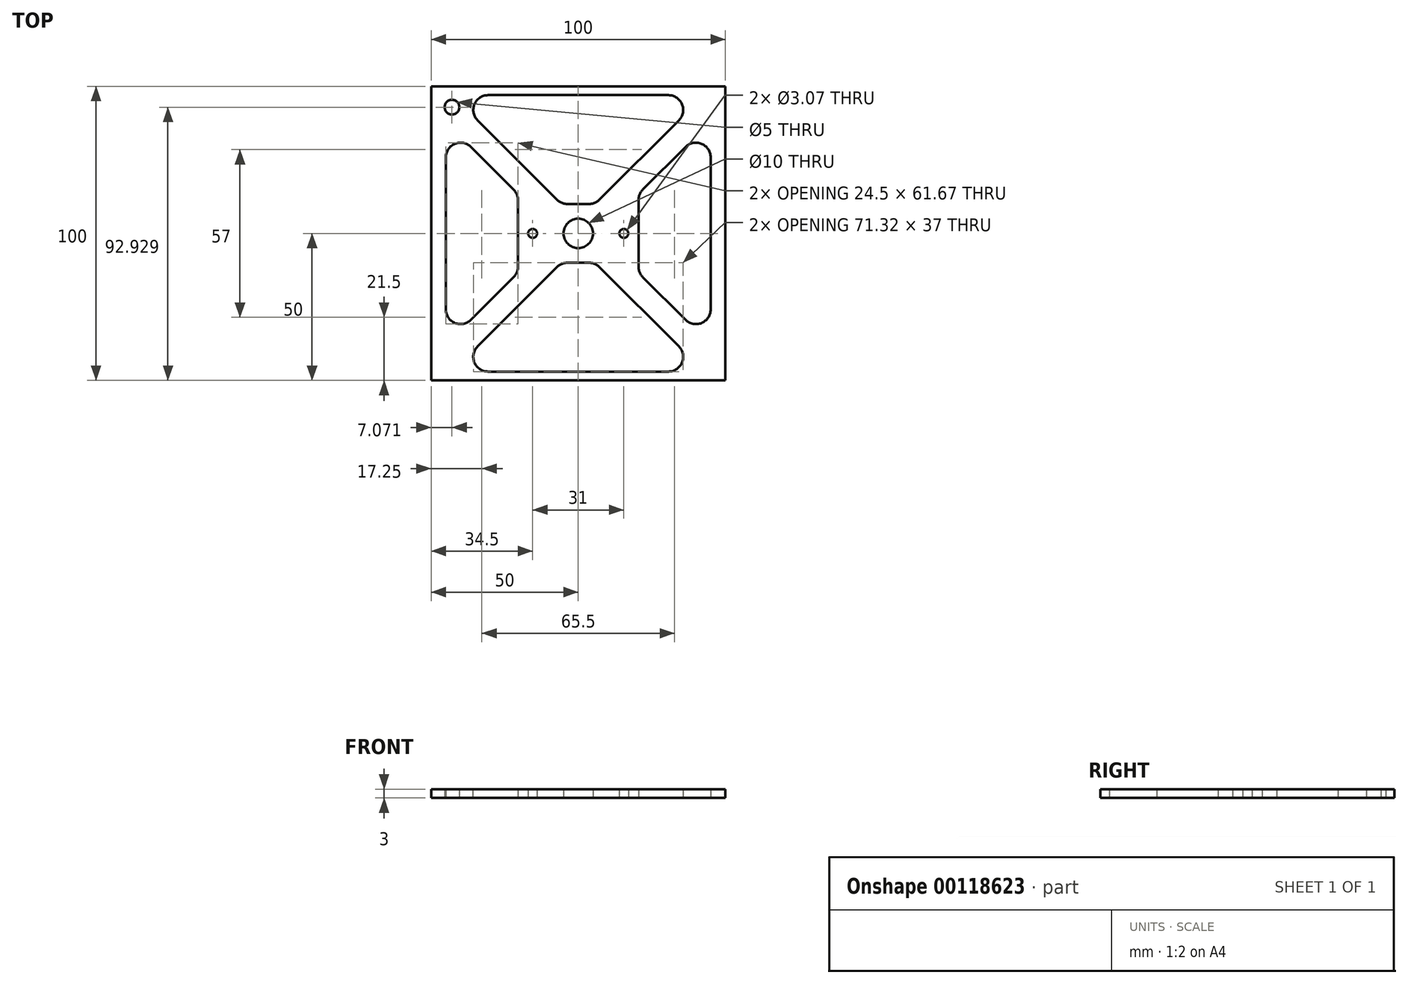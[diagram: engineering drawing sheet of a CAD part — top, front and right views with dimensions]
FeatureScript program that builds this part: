
annotation { "Feature Type Name" : "Feature", "Feature Type Description" : "" }
export const myFeature = defineFeature(function(context is Context, id is Id, definition is map)
    precondition{}
    {
        {
            var Q0;
            Q0=qCreatedBy(makeId("Top.planeOp"),FACE);
            var sketch = newSketch(context, id + "F0", { "sketchPlane" : qUnion([Q0])});
            skLineSegment(sketch, "E0.bottom", {"start": v(50, -50) * mm, "end": v(-50, -50) * mm});
            skLineSegment(sketch, "E0.top", {"start": v(50, 50) * mm, "end": v(-50, 50) * mm});
            skLineSegment(sketch, "E0.left", {"start": v(50, -50) * mm, "end": v(50, 50) * mm});
            skLineSegment(sketch, "E0.right", {"start": v(-50, -50) * mm, "end": v(-50, 50) * mm});
            skPoint(sketch, "E0.middle", {"position": v(0, 0) * mm});
            skCircle(sketch, "E1", {"center": v(0, 0) * mm, "radius": 5 * mm});
            skLineSegment(sketch, "E2", {"start": v(0, 0) * mm, "end": v(15.5, 0) * mm, "construction": true});
            skLineSegment(sketch, "E3", {"start": v(0, 0) * mm, "end": v(-15.5, 0) * mm, "construction": true});
            skCircle(sketch, "E4", {"center": v(-15.5, 0) * mm, "radius": 1.53 * mm});
            skCircle(sketch, "E5", {"center": v(15.5, 0) * mm, "radius": 1.53 * mm});
            skLineSegment(sketch, "E6", {"start": v(-50, 50) * mm, "end": v(-42.93, 42.93) * mm});
            skCircle(sketch, "E7", {"center": v(-42.93, 42.93) * mm, "radius": 2.5 * mm});
            skLineSegment(sketch, "E8", {"start": v(-50, -50) * mm, "end": v(0, 0) * mm, "construction": true});
            skLineSegment(sketch, "E9.0", {"start": v(-42.76, -47) * mm, "end": v(0, -4.24) * mm});
            skLineSegment(sketch, "E9.1", {"start": v(42.76, -47) * mm, "end": v(-42.76, -47) * mm});
            skLineSegment(sketch, "E9.2", {"start": v(42.76, -47) * mm, "end": v(0, -4.24) * mm});
            skLineSegment(sketch, "E10", {"start": v(0, 0) * mm, "end": v(0, -10) * mm, "construction": true});
            skLineSegment(sketch, "E11", {"start": v(0, -10) * mm, "end": v(5.76, -10) * mm});
            skLineSegment(sketch, "E12", {"start": v(0, -10) * mm, "end": v(-5.76, -10) * mm});
            skLineSegment(sketch, "E13", {"start": v(0, 0) * mm, "end": v(25, 0) * mm, "construction": true});
            skLineSegment(sketch, "E14", {"start": v(50, 50) * mm, "end": v(15.5, 15.5) * mm, "construction": true});
            skLineSegment(sketch, "E15", {"start": v(50, -50) * mm, "end": v(15.5, -15.5) * mm, "construction": true});
            skLineSegment(sketch, "E16", {"start": v(15.5, -15.5) * mm, "end": v(15.5, 15.5) * mm, "construction": true});
            skLineSegment(sketch, "E17.0", {"start": v(45, 37.93) * mm, "end": v(20.5, 13.43) * mm});
            skLineSegment(sketch, "E17.1", {"start": v(45, -37.93) * mm, "end": v(45, 37.93) * mm});
            skLineSegment(sketch, "E17.2", {"start": v(45, -37.93) * mm, "end": v(20.5, -13.43) * mm});
            skLineSegment(sketch, "E17.3", {"start": v(20.5, -13.43) * mm, "end": v(20.5, 13.43) * mm});
            skSolve(sketch);
        }
        {
            var Q0;
            Q0=makeQuery(id+"F0.imprint","IMPRINT",FACE,{"disambiguationData":[TD([[makeQuery(id+"F0.imprint","IMPRINT",EDGE,{"derivedFrom":sQuery(id+"F0.wireOp",EDGE,"E0.bottom")}),-1.0]])]});
            var Q1;
            {var subQ1=sQuery(id+"F0.wireOp",EDGE,"E9.1");Q1=makeQuery(id+"F0.imprint","IMPRINT",FACE,{"disambiguationData":[TD([[makeQuery(id+"F0.imprint","IMPRINT",EDGE,{"derivedFrom":subQ1}),-1.0]])]});}
            var Q2;
            {var subQ0=sQuery(id+"F0.wireOp",EDGE,"E11");Q2=makeQuery(id+"F0.imprint","IMPRINT",FACE,{"disambiguationData":[TD([[makeQuery(id+"F0.imprint","IMPRINT",EDGE,{"derivedFrom":subQ0}),1.0]])]});}
            extrude(context, id + "F1", {"entities" : qUnion([Q0, Q1, Q2]), "depth" : 3 * mm});
        }
        {
            var Q0;
            {var subQ1=sQuery(id+"F0.wireOp",EDGE,"E9.1");Q0=makeQuery(id+"F0.imprint","IMPRINT",FACE,{"disambiguationData":[TD([[makeQuery(id+"F0.imprint","IMPRINT",EDGE,{"derivedFrom":subQ1}),-1.0]])]});}
            extrude(context, id + "F2", {"entities" : qUnion([Q0]), "operationType" : NewBodyOperationType.REMOVE, "endBound" : BoundingType.THROUGH_ALL, "depth" : 25 * mm});
        }
        {
            var Q0;
            Q0=makeQuery(id+"F2.boolean.opBoolean","COPY",EDGE,{"derivedFrom":makeQuery(id+"F2.opExtrude","SWEPT_EDGE",EDGE,{"disambiguationData":[OSD([sQuery(id+"F0.wireOp",EDGE,"E9.2"),sQuery(id+"F0.wireOp",EDGE,"E11")])]})});
            var Q1;
            Q1=makeQuery(id+"F2.boolean.opBoolean","COPY",EDGE,{"derivedFrom":makeQuery(id+"F2.opExtrude","SWEPT_EDGE",EDGE,{"disambiguationData":[OSD([sQuery(id+"F0.wireOp",EDGE,"E9.0"),sQuery(id+"F0.wireOp",EDGE,"E12")])]})});
            var Q2;
            Q2=makeQuery(id+"F2.boolean.opBoolean","COPY",EDGE,{"derivedFrom":makeQuery(id+"F2.opExtrude","SWEPT_EDGE",EDGE,{"disambiguationData":[OSD([sQuery(id+"F0.wireOp",EDGE,"E9.1"),sQuery(id+"F0.wireOp",EDGE,"E9.2")])]})});
            var Q3;
            Q3=makeQuery(id+"F2.boolean.opBoolean","COPY",EDGE,{"derivedFrom":makeQuery(id+"F2.opExtrude","SWEPT_EDGE",EDGE,{"disambiguationData":[OSD([sQuery(id+"F0.wireOp",EDGE,"E9.0"),sQuery(id+"F0.wireOp",EDGE,"E9.1")])]})});
            fillet(context, id + "F3", {"entities" : qUnion([Q0, Q1, Q2, Q3]), "radius" : 5 * mm, "tangentPropagation" : true, "allowEdgeOverflow" : false});
        }
        {
            var Q0;
            Q0=makeQuery(id+"F3.opFillet","BLEND_FACE",FACE,{"disambiguationData":[OSD([sQuery(id+"F0.wireOp",EDGE,"E9.0"),sQuery(id+"F0.wireOp",EDGE,"E12")])]});
            var Q1;
            Q1=makeQuery(id+"F2.boolean.opBoolean","COPY",FACE,{"derivedFrom":makeQuery(id+"F2.opExtrude","SWEPT_FACE",FACE,{"disambiguationData":[OSD([sQuery(id+"F0.wireOp",EDGE,"E9.0")])]})});
            var Q2;
            Q2=makeQuery(id+"F2.boolean.opBoolean","COPY",FACE,{"derivedFrom":makeQuery(id+"F2.opExtrude","SWEPT_FACE",FACE,{"disambiguationData":[OSD([sQuery(id+"F0.wireOp",EDGE,"E11"),sQuery(id+"F0.wireOp",EDGE,"E12")])]})});
            var Q3;
            Q3=makeQuery(id+"F3.opFillet","BLEND_FACE",FACE,{"disambiguationData":[OSD([sQuery(id+"F0.wireOp",EDGE,"E9.2"),sQuery(id+"F0.wireOp",EDGE,"E11")])]});
            var Q4;
            Q4=makeQuery(id+"F2.boolean.opBoolean","COPY",FACE,{"derivedFrom":makeQuery(id+"F2.opExtrude","SWEPT_FACE",FACE,{"disambiguationData":[OSD([sQuery(id+"F0.wireOp",EDGE,"E9.2")])]})});
            var Q5;
            Q5=makeQuery(id+"F3.opFillet","BLEND_FACE",FACE,{"disambiguationData":[OSD([sQuery(id+"F0.wireOp",EDGE,"E9.0"),sQuery(id+"F0.wireOp",EDGE,"E9.1")])]});
            var Q6;
            Q6=makeQuery(id+"F2.boolean.opBoolean","COPY",FACE,{"derivedFrom":makeQuery(id+"F2.opExtrude","SWEPT_FACE",FACE,{"disambiguationData":[OSD([sQuery(id+"F0.wireOp",EDGE,"E9.1")])]})});
            var Q7;
            Q7=makeQuery(id+"F3.opFillet","BLEND_FACE",FACE,{"disambiguationData":[OSD([sQuery(id+"F0.wireOp",EDGE,"E9.1"),sQuery(id+"F0.wireOp",EDGE,"E9.2")])]});
            var Q8;
            Q8=qCreatedBy(makeId("Front.planeOp"),FACE);
            mirror(context, id + "F4", {"faces" : qUnion([Q0, Q1, Q2, Q3, Q4, Q5, Q6, Q7]), "mirrorPlane" : qUnion([Q8]), "patternType" : MirrorType.FACE});
        }
        {
            var Q0;
            Q0=makeQuery(id+"F1.opExtrude","SWEPT_EDGE",EDGE,{"disambiguationData":[OSD([sQuery(id+"F0.wireOp",EDGE,"E17.0"),sQuery(id+"F0.wireOp",EDGE,"E17.1")])]});
            var Q1;
            Q1=makeQuery(id+"F1.opExtrude","SWEPT_EDGE",EDGE,{"disambiguationData":[OSD([sQuery(id+"F0.wireOp",EDGE,"E17.2"),sQuery(id+"F0.wireOp",EDGE,"E17.3")])]});
            var Q2;
            Q2=makeQuery(id+"F1.opExtrude","SWEPT_EDGE",EDGE,{"disambiguationData":[OSD([sQuery(id+"F0.wireOp",EDGE,"E17.1"),sQuery(id+"F0.wireOp",EDGE,"E17.2")])]});
            var Q3;
            Q3=makeQuery(id+"F1.opExtrude","SWEPT_EDGE",EDGE,{"disambiguationData":[OSD([sQuery(id+"F0.wireOp",EDGE,"E17.0"),sQuery(id+"F0.wireOp",EDGE,"E17.3")])]});
            fillet(context, id + "F5", {"entities" : qUnion([Q0, Q1, Q2, Q3]), "radius" : 5 * mm, "tangentPropagation" : true, "allowEdgeOverflow" : false});
        }
        {
            var Q0;
            Q0=makeQuery(id+"F1.opExtrude","SWEPT_FACE",FACE,{"disambiguationData":[OSD([sQuery(id+"F0.wireOp",EDGE,"E17.1")])]});
            var Q1;
            Q1=makeQuery(id+"F5.opFillet","BLEND_FACE",FACE,{"disambiguationData":[OSD([sQuery(id+"F0.wireOp",EDGE,"E17.0"),sQuery(id+"F0.wireOp",EDGE,"E17.1")])]});
            var Q2;
            Q2=makeQuery(id+"F5.opFillet","BLEND_FACE",FACE,{"disambiguationData":[OSD([sQuery(id+"F0.wireOp",EDGE,"E17.1"),sQuery(id+"F0.wireOp",EDGE,"E17.2")])]});
            var Q3;
            Q3=makeQuery(id+"F1.opExtrude","SWEPT_FACE",FACE,{"disambiguationData":[OSD([sQuery(id+"F0.wireOp",EDGE,"E17.2")])]});
            var Q4;
            Q4=makeQuery(id+"F5.opFillet","BLEND_FACE",FACE,{"disambiguationData":[OSD([sQuery(id+"F0.wireOp",EDGE,"E17.2"),sQuery(id+"F0.wireOp",EDGE,"E17.3")])]});
            var Q5;
            Q5=makeQuery(id+"F1.opExtrude","SWEPT_FACE",FACE,{"disambiguationData":[OSD([sQuery(id+"F0.wireOp",EDGE,"E17.3")])]});
            var Q6;
            Q6=makeQuery(id+"F5.opFillet","BLEND_FACE",FACE,{"disambiguationData":[OSD([sQuery(id+"F0.wireOp",EDGE,"E17.0"),sQuery(id+"F0.wireOp",EDGE,"E17.3")])]});
            var Q7;
            Q7=makeQuery(id+"F1.opExtrude","SWEPT_FACE",FACE,{"disambiguationData":[OSD([sQuery(id+"F0.wireOp",EDGE,"E17.0")])]});
            var Q8;
            Q8=qCreatedBy(makeId("Right.planeOp"),FACE);
            mirror(context, id + "F6", {"faces" : qUnion([Q0, Q1, Q2, Q3, Q4, Q5, Q6, Q7]), "mirrorPlane" : qUnion([Q8]), "patternType" : MirrorType.FACE});
        }
    });
